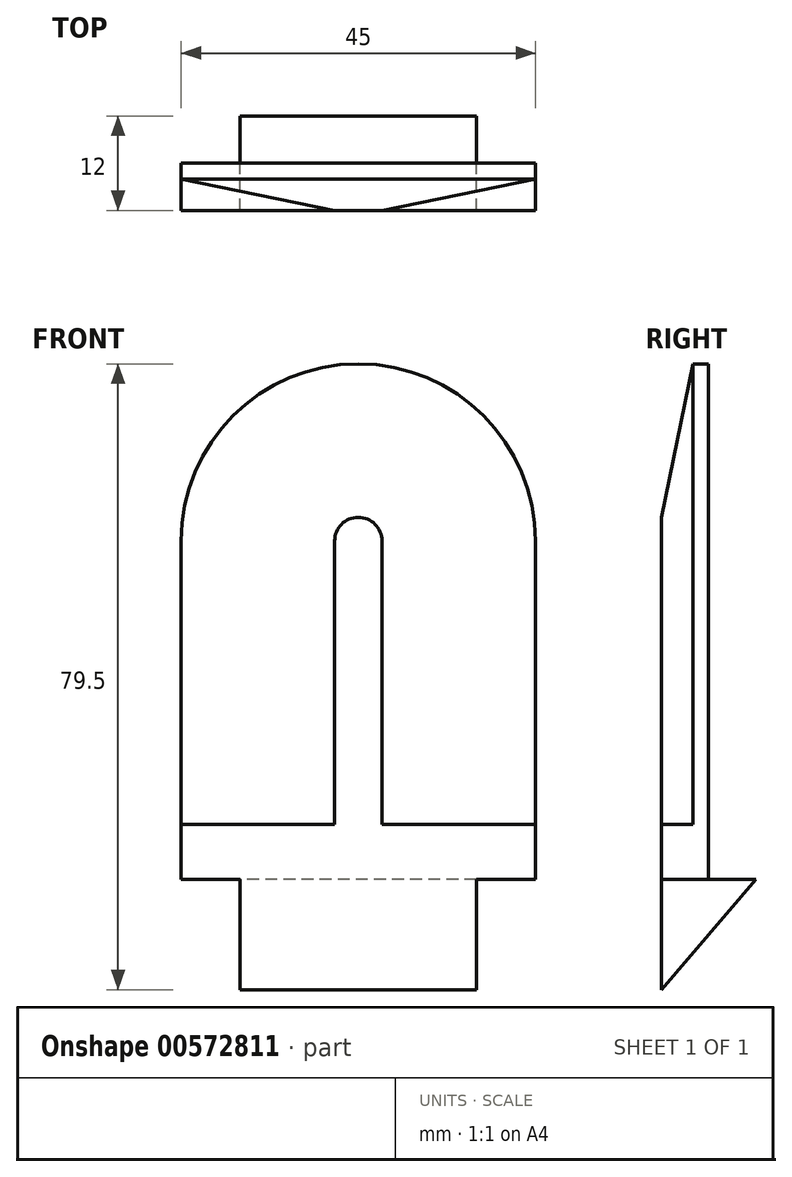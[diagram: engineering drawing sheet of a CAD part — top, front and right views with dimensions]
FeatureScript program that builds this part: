
annotation { "Feature Type Name" : "Feature", "Feature Type Description" : "" }
export const myFeature = defineFeature(function(context is Context, id is Id, definition is map)
    precondition{}
    {
        {
            var Q0;
            Q0=qCreatedBy(makeId("Front.planeOp"),FACE);
            var sketch = newSketch(context, id + "F0", { "sketchPlane" : qUnion([Q0])});
            skLineSegment(sketch, "E0.bottom", {"start": v(-22.5, 21.5) * mm, "end": v(22.5, 21.5) * mm});
            skLineSegment(sketch, "E0.top", {"start": v(-22.5, -21.5) * mm, "end": v(22.5, -21.5) * mm});
            skLineSegment(sketch, "E0.left", {"start": v(-22.5, 21.5) * mm, "end": v(-22.5, -21.5) * mm});
            skLineSegment(sketch, "E0.right", {"start": v(22.5, 21.5) * mm, "end": v(22.5, -21.5) * mm});
            skPoint(sketch, "E0.middle", {"position": v(0, 0) * mm});
            skLineSegment(sketch, "E1", {"start": v(0, 21.5) * mm, "end": v(0, 44) * mm});
            skPoint(sketch, "E1.endSnap0", {"position": v(0, 21.5) * mm});
            skCircle(sketch, "E2", {"center": v(0, 21.5) * mm, "radius": 22.5 * mm});
            skLineSegment(sketch, "E3", {"start": v(0, 44) * mm, "end": v(0, -21.5) * mm});
            skSolve(sketch);
        }
        {
            var Q0;
            Q0 = qSketchRegion(id + "F0", true);
            extrude(context, id + "F1", {"entities" : qUnion([Q0]), "depth" : 6 * mm, "offsetDistance" : 25 * mm});
        }
        {
            var Q0;
            Q0=makeQuery(id+"F1.opExtrude","CAP_EDGE",EDGE,{"disambiguationData":[OSD([sQuery(id+"F0.wireOp",EDGE,"E2")])],"isStart":false});
            chamfer(context, id + "F2", {"entities" : qUnion([Q0]), "chamferType" : ChamferType.TWO_OFFSETS, "width1" : 19.5 * mm, "oppositeDirection" : false, "width2" : 4 * mm, "tangentPropagation" : true});
        }
        {
            var Q0;
            Q0=makeQuery(id+"F1.opExtrude","CAP_FACE",FACE,{"disambiguationData":[OSD([sQuery(id+"F0.wireOp",EDGE,"E0.top"),sQuery(id+"F0.wireOp",EDGE,"E0.left"),sQuery(id+"F0.wireOp",EDGE,"E0.right"),sQuery(id+"F0.wireOp",EDGE,"E2")])],"isStart":true});
            var sketch = newSketch(context, id + "F3", { "sketchPlane" : qUnion([Q0])});
            skLineSegment(sketch, "E4.bottom", {"start": v(-22.5, -21.5) * mm, "end": v(22.5, -21.5) * mm});
            skLineSegment(sketch, "E4.top", {"start": v(-22.5, -14.5) * mm, "end": v(22.5, -14.5) * mm});
            skLineSegment(sketch, "E4.left", {"start": v(-22.5, -21.5) * mm, "end": v(-22.5, -14.5) * mm});
            skLineSegment(sketch, "E4.right", {"start": v(22.5, -21.5) * mm, "end": v(22.5, -14.5) * mm});
            skSolve(sketch);
        }
        {
            var Q0;
            Q0=makeQuery(id+"F3.imprint","IMPRINT",FACE,{"disambiguationData":[TD([[makeQuery(id+"F3.imprint","IMPRINT",EDGE,{"derivedFrom":sQuery(id+"F3.wireOp",EDGE,"E4.bottom")}),-1.0]])]});
            extrude(context, id + "F4", {"entities" : qUnion([Q0]), "operationType" : NewBodyOperationType.ADD, "oppositeDirection" : true, "depth" : 6 * mm, "offsetDistance" : 25 * mm});
        }
        {
            var Q0;
            Q0=makeQuery(id+"F4.boolean.opBoolean","MERGE",FACE,{"derivedFrom":[makeQuery(id+"F1.opExtrude","SWEPT_FACE",FACE,{"disambiguationData":[OSD([sQuery(id+"F0.wireOp",EDGE,"E0.top")])]}),makeQuery(id+"F4.opExtrude","SWEPT_FACE",FACE,{"disambiguationData":[OSD([sQuery(id+"F3.wireOp",EDGE,"E4.bottom")])]})]});
            var sketch = newSketch(context, id + "F5", { "sketchPlane" : qUnion([Q0])});
            skLineSegment(sketch, "E5", {"start": v(-22.5, 6) * mm, "end": v(-15, 6) * mm});
            skLineSegment(sketch, "E6", {"start": v(22.5, 6) * mm, "end": v(15, 6) * mm});
            skLineSegment(sketch, "E7.bottom", {"start": v(-15, 6) * mm, "end": v(15, 6) * mm});
            skLineSegment(sketch, "E7.top", {"start": v(-15, 0) * mm, "end": v(15, 0) * mm});
            skLineSegment(sketch, "E7.left", {"start": v(-15, 6) * mm, "end": v(-15, 0) * mm});
            skLineSegment(sketch, "E7.right", {"start": v(15, 6) * mm, "end": v(15, 0) * mm});
            skSolve(sketch);
        }
        {
            var Q0;
            Q0 = qSketchRegion(id + "F5", true);
            var Q1;
            Q1=makeQuery(id+"F5.imprint","IMPRINT",FACE,{"disambiguationData":[TD([[makeQuery(id+"F5.imprint","IMPRINT",EDGE,{"derivedFrom":sQuery(id+"F5.wireOp",EDGE,"E7.bottom")}),-1.0]])]});
            extrude(context, id + "F6", {"entities" : qUnion([Q0, Q1]), "operationType" : NewBodyOperationType.ADD, "depth" : 14 * mm, "offsetDistance" : 25 * mm});
        }
        {
            var Q0;
            Q0=makeQuery(id+"F6.boolean.opBoolean","MERGE",FACE,{"derivedFrom":[makeQuery(id+"F1.opExtrude","CAP_FACE",FACE,{"disambiguationData":[OSD([sQuery(id+"F0.wireOp",EDGE,"E0.top"),sQuery(id+"F0.wireOp",EDGE,"E0.left"),sQuery(id+"F0.wireOp",EDGE,"E0.right"),sQuery(id+"F0.wireOp",EDGE,"E2")])],"isStart":true}),makeQuery(id+"F6.opExtrude","SWEPT_FACE",FACE,{"disambiguationData":[OSD([sQuery(id+"F5.wireOp",EDGE,"E7.top")])]})]});
            var sketch = newSketch(context, id + "F7", { "sketchPlane" : qUnion([Q0])});
            skLineSegment(sketch, "E8.bottom", {"start": v(-15, -35.5) * mm, "end": v(15, -35.5) * mm});
            skLineSegment(sketch, "E8.top", {"start": v(-15, -21.5) * mm, "end": v(15, -21.5) * mm});
            skLineSegment(sketch, "E8.left", {"start": v(-15, -35.5) * mm, "end": v(-15, -21.5) * mm});
            skLineSegment(sketch, "E8.right", {"start": v(15, -35.5) * mm, "end": v(15, -21.5) * mm});
            skSolve(sketch);
        }
        {
            var Q0;
            Q0 = qSketchRegion(id + "F7", true);
            extrude(context, id + "F8", {"entities" : qUnion([Q0]), "operationType" : NewBodyOperationType.ADD, "depth" : 6 * mm, "offsetDistance" : 25 * mm});
        }
        {
            var Q0;
            Q0=makeQuery(id+"F8.opExtrude","CAP_EDGE",EDGE,{"disambiguationData":[OSD([sQuery(id+"F7.wireOp",EDGE,"E8.bottom")])],"isStart":false});
            chamfer(context, id + "F9", {"entities" : qUnion([Q0]), "chamferType" : ChamferType.TWO_OFFSETS, "width1" : 12 * mm, "oppositeDirection" : false, "width2" : 14 * mm, "tangentPropagation" : true});
        }
    });
